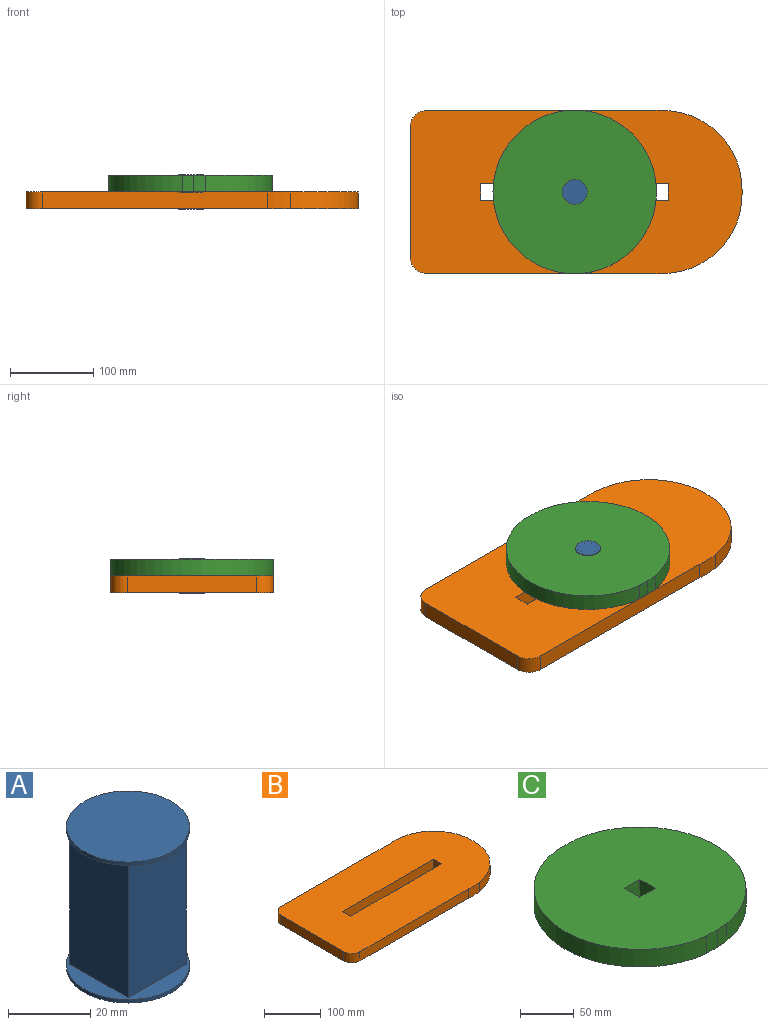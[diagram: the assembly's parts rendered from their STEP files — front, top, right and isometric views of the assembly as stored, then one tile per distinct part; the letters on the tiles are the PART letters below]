
ASSEMBLY  parts=3 mates=2
PART A: 10 faces, bbox 30x30x42 mm
  f0: plane 30x30mm, normal (0,0,-1), area 306.9mm2, adj f1,f6,f7,f8,f9
  f1: cylinder r=15mm len=30mm, axis (0,0,-1), area 94.2mm2, adj f0,f2
  f2: plane 30x30mm, normal (0,0,1), area 706.9mm2, adj f1
  f3: plane 30x30mm, normal (0,0,1), area 306.9mm2, adj f4,f6,f7,f8,f9
  f4: cylinder r=15mm len=30mm, axis (0,0,-1), area 94.2mm2, adj f3,f5
  f5: plane 30x30mm, normal (0,0,-1), area 706.9mm2, adj f4
  f6: plane 40x20mm, normal (0,1,0), area 800mm2, adj f0,f3,f7,f9
  f7: plane 40x20mm, normal (-1,0,0), area 800mm2, adj f0,f3,f6,f8
  f8: plane 40x20mm, normal (0,-1,0), area 800mm2, adj f0,f3,f7,f9
  f9: plane 40x20mm, normal (1,0,0), area 800mm2, adj f0,f3,f6,f8
PART B: 16 faces, bbox 400x197.1x20 mm
  f0: plane 20x20mm, normal (-1,0,0), area 400mm2, adj f1,f13,f14,f15
  f1: plane 226.39x20mm, normal (0,1,0), area 4527.8mm2, adj f0,f2,f14,f15
  f2: plane 20x20mm, normal (1,0,0), area 400mm2, adj f1,f13,f14,f15
  f3: cylinder r=95mm len=94.03mm, axis (0,0,-1), area 2712.5mm2, adj f4,f12,f14,f15
  f4: cylinder r=98.53mm len=27.42mm, axis (0,0,-1), area 550.5mm2, adj f3,f5,f14,f15
  f5: plane 271.13x20mm, normal (0,1,0), area 5422.7mm2, adj f4,f6,f14,f15
  f6: cylinder r=20mm len=20mm, axis (0,0,-1), area 628.3mm2, adj f5,f7,f14,f15
  f7: plane 156x20mm, normal (-1,0,0), area 3120mm2, adj f6,f8,f14,f15
  f8: cylinder r=20mm len=20mm, axis (0,0,-1), area 628.3mm2, adj f7,f9,f14,f15
  f9: plane 271.13x20mm, normal (0,-1,0), area 5422.7mm2, adj f8,f10,f14,f15
  f10: cylinder r=98.53mm len=27.42mm, axis (0,0,-1), area 550.5mm2, adj f9,f11,f14,f15
  f11: cylinder r=95mm len=94.03mm, axis (0,0,-1), area 2712.5mm2, adj f10,f12,f14,f15
  f12: plane 20x6mm, normal (1,0,0), area 120mm2, adj f3,f11,f14,f15
  f13: plane 226.39x20mm, normal (0,-1,0), area 4527.8mm2, adj f0,f2,f14,f15
  f14: plane 400x197.07mm, normal (0,0,1), area 69844.3mm2, adj f0,f1,f2,f3,f4,f5,f6,f7
  f15: plane 400x197.07mm, normal (0,0,-1), area 69844.3mm2, adj f0,f1,f2,f3,f4,f5,f6,f7
PART C: 12 faces, bbox 197.1x196x20 mm
  f0: plane 20x20mm, normal (0,1,0), area 400mm2, adj f1,f9,f10,f11
  f1: plane 20x20mm, normal (1,0,0), area 400mm2, adj f0,f2,f10,f11
  f2: plane 20x20mm, normal (0,-1,0), area 400mm2, adj f1,f9,f10,f11
  f3: plane 20x13.87mm, normal (0,1,0), area 277.3mm2, adj f4,f8,f10,f11
  f4: cylinder r=98.53mm len=196mm, axis (0,0,-1), area 5780.2mm2, adj f3,f5,f10,f11
  f5: plane 20x13.87mm, normal (0,-1,0), area 277.3mm2, adj f4,f6,f10,f11
  f6: cylinder r=95mm len=20mm, axis (0,0,-1), area 272mm2, adj f5,f7,f10,f11
  f7: cylinder r=98.53mm len=194.06mm, axis (0,0,-1), area 5501mm2, adj f6,f8,f10,f11
  f8: cylinder r=95mm len=20mm, axis (0,0,-1), area 272mm2, adj f3,f7,f10,f11
  f9: plane 20x20mm, normal (-1,0,0), area 400mm2, adj f0,f2,f10,f11
  f10: plane 197.07x196mm, normal (0,0,1), area 30084.9mm2, adj f0,f1,f2,f3,f4,f5,f6,f7
  f11: plane 197.07x196mm, normal (0,0,-1), area 30084.9mm2, adj f0,f1,f2,f3,f4,f5,f6,f7
PLACE A rot(axis=(0,0,-1),0deg) t=(-272.9,3.66,-21.41)mm
PLACE B t=(-170.03,3.66,-21.41)mm fixed
PLACE C t=(-272.9,3.66,-1.41)mm
MATE fastened C.f4 <-> A.f1  axis (0,0,-1) through (-171.51,3.66,-1.41)mm
MATE pin_slot A.f1 <-> B.f15  axis (0,0,1) through (-171.51,3.66,-21.41)mm
